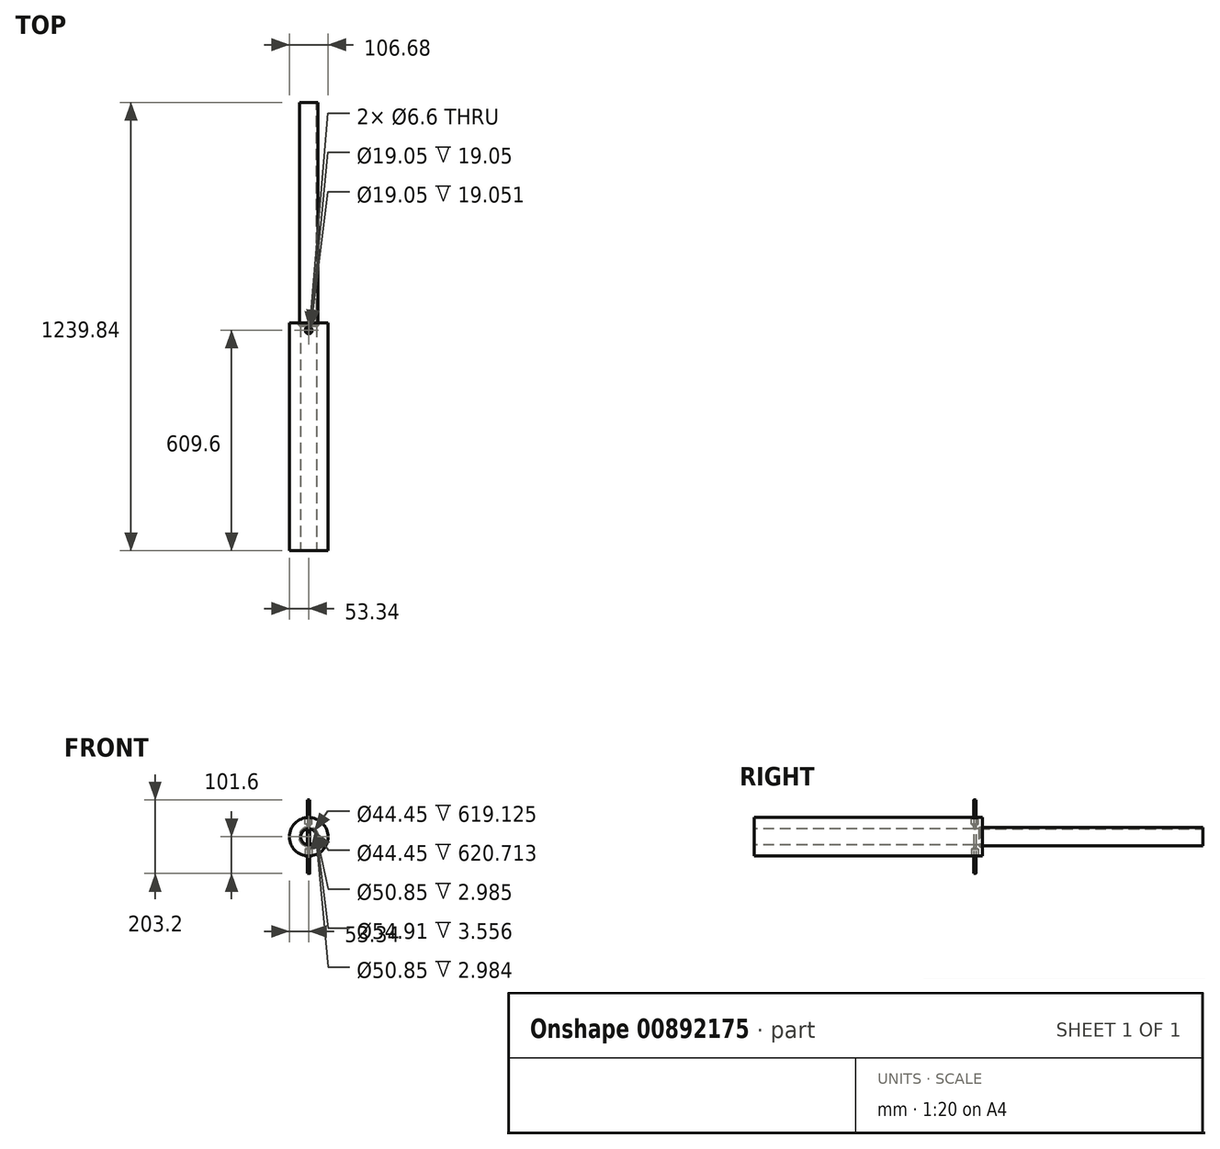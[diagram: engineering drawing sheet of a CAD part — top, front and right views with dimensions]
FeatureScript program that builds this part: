
annotation { "Feature Type Name" : "Feature", "Feature Type Description" : "" }
export const myFeature = defineFeature(function(context is Context, id is Id, definition is map)
    precondition{}
    {
        {
            var Q0;
            Q0=qCreatedBy(makeId("Front.planeOp"),FACE);
            var sketch = newSketch(context, id + "F0", { "sketchPlane" : qUnion([Q0])});
            skCircle(sketch, "E0", {"center": v(0, 0) * mm, "radius": 22.23 * mm});
            skCircle(sketch, "E1", {"center": v(0, 0) * mm, "radius": 53.34 * mm});
            skSolve(sketch);
        }
        {
            var Q0;
            Q0=makeQuery(id+"F0.imprint","IMPRINT",FACE,{"disambiguationData":[TD([[makeQuery(id+"F0.imprint","IMPRINT",EDGE,{"derivedFrom":sQuery(id+"F0.wireOp",EDGE,"E0")}),-1.0]])]});
            extrude(context, id + "F1", {"entities" : qUnion([Q0]), "oppositeDirection" : true, "depth" : 20.64 * mm, "offsetDistance" : 25.4 * mm});
        }
        {
            var Q0;
            Q0=qCreatedBy(makeId("Top.planeOp"),FACE);
            cPlane(context, id + "F2", {"entities" : qUnion([Q0]), "cplaneType" : CPlaneType.OFFSET, "offset" : 53.34 * mm, "width" : 152.4 * mm, "height" : 152.4 * mm});
        }
        {
            var Q0;
            Q0=qCreatedBy(makeId("Top.planeOp"),FACE);
            cPlane(context, id + "F3", {"entities" : qUnion([Q0]), "cplaneType" : CPlaneType.OFFSET, "offset" : 53.34 * mm, "oppositeDirection" : true, "width" : 152.4 * mm, "height" : 152.4 * mm});
        }
        {
            var Q0;
            Q0=qCreatedBy(id+"F2.planeOp",FACE);
            var sketch = newSketch(context, id + "F4", { "sketchPlane" : qUnion([Q0])});
            skCircle(sketch, "E2", {"center": v(0, 0) * mm, "radius": 9.53 * mm});
            skCircle(sketch, "E3", {"center": v(0, 0) * mm, "radius": 3.3 * mm});
            skSolve(sketch);
        }
        {
            var Q0;
            Q0=qCreatedBy(id+"F3.planeOp",FACE);
            var sketch = newSketch(context, id + "F5", { "sketchPlane" : qUnion([Q0])});
            skCircle(sketch, "E4", {"center": v(0, 0) * mm, "radius": 9.53 * mm});
            skCircle(sketch, "E5", {"center": v(0, 0) * mm, "radius": 3.3 * mm});
            skSolve(sketch);
        }
        {
            var Q0;
            Q0=makeQuery(id+"F0.imprint","IMPRINT",FACE,{"disambiguationData":[TD([[makeQuery(id+"F0.imprint","IMPRINT",EDGE,{"derivedFrom":sQuery(id+"F0.wireOp",EDGE,"E0")}),-1.0]])]});
            extrude(context, id + "F6", {"entities" : qUnion([Q0]), "operationType" : NewBodyOperationType.ADD, "depth" : 609.6 * mm, "offsetDistance" : 25.4 * mm});
        }
        {
            var Q0;
            Q0=makeQuery(id+"F5.imprint","IMPRINT",FACE,{"disambiguationData":[TD([[makeQuery(id+"F5.imprint","IMPRINT",EDGE,{"derivedFrom":sQuery(id+"F5.wireOp",EDGE,"E5")}),1.0]])]});
            var Q1;
            Q1=makeQuery(id+"F5.imprint","IMPRINT",FACE,{"disambiguationData":[TD([[makeQuery(id+"F5.imprint","IMPRINT",EDGE,{"derivedFrom":sQuery(id+"F5.wireOp",EDGE,"E4")}),1.0]])]});
            extrude(context, id + "F7", {"entities" : qUnion([Q0, Q1]), "operationType" : NewBodyOperationType.REMOVE, "depth" : 19.05 * mm, "offsetDistance" : 25.4 * mm});
        }
        {
            var Q0;
            Q0=makeQuery(id+"F5.imprint","IMPRINT",FACE,{"disambiguationData":[TD([[makeQuery(id+"F5.imprint","IMPRINT",EDGE,{"derivedFrom":sQuery(id+"F5.wireOp",EDGE,"E5")}),1.0]])]});
            var Q1;
            {var subQ0=sQuery(id+"F0.wireOp",EDGE,"E0");Q1=makeQuery(id+"F6.boolean.opBoolean","MERGE",FACE,{"derivedFrom":[makeQuery(id+"F1.opExtrude","SWEPT_FACE",FACE,{"disambiguationData":[OSD([subQ0])]}),makeQuery(id+"F6.opExtrude","SWEPT_FACE",FACE,{"disambiguationData":[OSD([subQ0])]})]});}
            extrude(context, id + "F8", {"entities" : qUnion([Q0]), "operationType" : NewBodyOperationType.REMOVE, "endBound" : BoundingType.UP_TO_SURFACE, "depth" : 25.4 * mm, "endBoundEntityFace" : qUnion([Q1]), "offsetDistance" : 25.4 * mm});
        }
        {
            var Q0;
            Q0=makeQuery(id+"F4.imprint","IMPRINT",FACE,{"disambiguationData":[TD([[makeQuery(id+"F4.imprint","IMPRINT",EDGE,{"derivedFrom":sQuery(id+"F4.wireOp",EDGE,"E2")}),1.0]])]});
            var Q1;
            Q1=makeQuery(id+"F4.imprint","IMPRINT",FACE,{"disambiguationData":[TD([[makeQuery(id+"F4.imprint","IMPRINT",EDGE,{"derivedFrom":sQuery(id+"F4.wireOp",EDGE,"E3")}),1.0]])]});
            extrude(context, id + "F9", {"entities" : qUnion([Q0, Q1]), "operationType" : NewBodyOperationType.REMOVE, "oppositeDirection" : true, "depth" : 19.05 * mm, "offsetDistance" : 25.4 * mm});
        }
        {
            var Q0;
            Q0=makeQuery(id+"F4.imprint","IMPRINT",FACE,{"disambiguationData":[TD([[makeQuery(id+"F4.imprint","IMPRINT",EDGE,{"derivedFrom":sQuery(id+"F4.wireOp",EDGE,"E3")}),1.0]])]});
            var Q1;
            {var subQ0=sQuery(id+"F0.wireOp",EDGE,"E0");Q1=makeQuery(id+"F6.boolean.opBoolean","MERGE",FACE,{"derivedFrom":[makeQuery(id+"F1.opExtrude","SWEPT_FACE",FACE,{"disambiguationData":[OSD([subQ0])]}),makeQuery(id+"F6.opExtrude","SWEPT_FACE",FACE,{"disambiguationData":[OSD([subQ0])]})]});}
            extrude(context, id + "F10", {"entities" : qUnion([Q0]), "operationType" : NewBodyOperationType.REMOVE, "endBound" : BoundingType.UP_TO_SURFACE, "oppositeDirection" : true, "depth" : 25.4 * mm, "endBoundEntityFace" : qUnion([Q1]), "offsetDistance" : 25.4 * mm});
        }
        {
            var Q0;
            Q0=qCreatedBy(makeId("Right.planeOp"),FACE);
            var sketch = newSketch(context, id + "F11", { "sketchPlane" : qUnion([Q0])});
            skLineSegment(sketch, "E6", {"start": v(0, 0) * mm, "end": v(3.3, 0) * mm});
            skLineSegment(sketch, "E7", {"start": v(3.3, 34.3) * mm, "end": v(6.35, 34.3) * mm});
            skLineSegment(sketch, "E8", {"start": v(3.3, 29.21) * mm, "end": v(6.35, 34.3) * mm});
            skLineSegment(sketch, "E9", {"start": v(3.3, -34.3) * mm, "end": v(6.35, -34.3) * mm});
            skLineSegment(sketch, "E10", {"start": v(3.3, -29.21) * mm, "end": v(6.35, -34.3) * mm});
            skLineSegment(sketch, "E11", {"start": v(0, 0) * mm, "end": v(0, 13.94) * mm});
            skLineSegment(sketch, "E12", {"start": v(0, 13.94) * mm, "end": v(0, -17.8) * mm});
            skLineSegment(sketch, "E13", {"start": v(3.3, 34.3) * mm, "end": v(3.3, 29.21) * mm});
            skLineSegment(sketch, "E14", {"start": v(3.3, -29.21) * mm, "end": v(3.3, -34.3) * mm});
            skSolve(sketch);
        }
        {
            var Q0;
            Q0 = qSketchRegion(id + "F11", true);
            var Q1;
            Q1=sQuery(id+"F11.wireOp",EDGE,"E11");
            revolve(context, id + "F12", {"operationType" : NewBodyOperationType.REMOVE, "surfaceOperationType" : NewSurfaceOperationType.NEW, "entities" : qUnion([Q0]), "axis" : qUnion([Q1]), "revolveType" : RevolveType.FULL, "oppositeDirection" : true});
        }
        {
            var Q0;
            Q0=qCreatedBy(makeId("Top.planeOp"),FACE);
            var sketch = newSketch(context, id + "F13", { "sketchPlane" : qUnion([Q0])});
            skLineSegment(sketch, "E15", {"start": v(0, 0) * mm, "end": v(0, 11.11) * mm});
            skLineSegment(sketch, "E16", {"start": v(0, 11.11) * mm, "end": v(-22.23, 11.11) * mm});
            skLineSegment(sketch, "E17", {"start": v(-22.23, 11.11) * mm, "end": v(-22.23, 20.64) * mm});
            skLineSegment(sketch, "E18", {"start": v(-22.23, 20.64) * mm, "end": v(-25.43, 20.64) * mm});
            skLineSegment(sketch, "E19", {"start": v(-25.43, 20.64) * mm, "end": v(-25.43, 11.11) * mm});
            skLineSegment(sketch, "E20", {"start": v(-25.43, 11.11) * mm, "end": v(-22.23, 11.11) * mm});
            skLineSegment(sketch, "E21", {"start": v(-27.46, 14.1) * mm, "end": v(-25.43, 14.1) * mm});
            skLineSegment(sketch, "E22", {"start": v(-27.46, 14.1) * mm, "end": v(-27.46, 17.65) * mm});
            skLineSegment(sketch, "E23", {"start": v(-27.46, 17.65) * mm, "end": v(-25.43, 17.65) * mm});
            skSolve(sketch);
        }
        {
            var Q0;
            Q0 = qSketchRegion(id + "F13", true);
            var Q1;
            Q1=sQuery(id+"F13.wireOp",EDGE,"E15");
            revolve(context, id + "F14", {"operationType" : NewBodyOperationType.REMOVE, "surfaceOperationType" : NewSurfaceOperationType.NEW, "entities" : qUnion([Q0]), "axis" : qUnion([Q1]), "revolveType" : RevolveType.FULL, "oppositeDirection" : true});
        }
        {
            var Q0;
            Q0=qCreatedBy(makeId("Top.planeOp"),FACE);
            var sketch = newSketch(context, id + "F15", { "sketchPlane" : qUnion([Q0])});
            skCircle(sketch, "E24", {"center": v(0, 0) * mm, "radius": 3.18 * mm});
            skSolve(sketch);
        }
        {
            var Q0;
            Q0=makeQuery(id+"F15.imprint","IMPRINT",FACE,{"disambiguationData":[TD([[makeQuery(id+"F15.imprint","IMPRINT",EDGE,{"derivedFrom":sQuery(id+"F15.wireOp",EDGE,"E24")}),1.0]])]});
            extrude(context, id + "F16", {"entities" : qUnion([Q0]), "endBound" : BoundingType.SYMMETRIC, "depth" : 203.2 * mm, "offsetDistance" : 25.4 * mm});
        }
        {
            var Q0;
            Q0=qCreatedBy(makeId("Top.planeOp"),FACE);
            var sketch = newSketch(context, id + "F17", { "sketchPlane" : qUnion([Q0])});
            skLineSegment(sketch, "E25", {"start": v(0, 0) * mm, "end": v(0, 18.94) * mm, "construction": true});
            skCircle(sketch, "E26", {"center": v(-26.34, 15.88) * mm, "radius": 1.12 * mm});
            skSolve(sketch);
        }
        {
            var Q0;
            Q0=sQuery(id+"F17.wireOp",EDGE,"E26");
            var Q1;
            Q1=sQuery(id+"F17.wireOp",EDGE,"E25");
            revolve(context, id + "F18", {"bodyType" : ToolBodyType.SURFACE, "surfaceOperationType" : NewSurfaceOperationType.NEW, "surfaceEntities" : qUnion([Q0]), "axis" : qUnion([Q1]), "revolveType" : RevolveType.FULL});
        }
        {
            var Q0;
            Q0=makeQuery(id+"F1.opExtrude","CAP_FACE",FACE,{"disambiguationData":[OSD([sQuery(id+"F0.wireOp",EDGE,"E0"),sQuery(id+"F0.wireOp",EDGE,"E1")])],"isStart":false});
            var sketch = newSketch(context, id + "F19", { "sketchPlane" : qUnion([Q0])});
            skCircle(sketch, "E27", {"center": v(0, 0) * mm, "radius": 25.4 * mm});
            skCircle(sketch, "E28", {"center": v(0, 0) * mm, "radius": 22.23 * mm});
            skSolve(sketch);
        }
        {
            var Q0;
            Q0 = qSketchRegion(id + "F19", true);
            extrude(context, id + "F20", {"entities" : qUnion([Q0]), "oppositeDirection" : true, "depth" : 9.52 * mm, "offsetDistance" : 25.4 * mm});
        }
        {
            var Q0;
            Q0=makeQuery(id+"F20.opExtrude","CAP_FACE",FACE,{"disambiguationData":[OSD([sQuery(id+"F19.wireOp",EDGE,"E27"),sQuery(id+"F19.wireOp",EDGE,"E28")])],"isStart":true});
            extrude(context, id + "F21", {"entities" : qUnion([Q0]), "operationType" : NewBodyOperationType.ADD, "depth" : 609.6 * mm, "offsetDistance" : 25.4 * mm});
        }
    });
